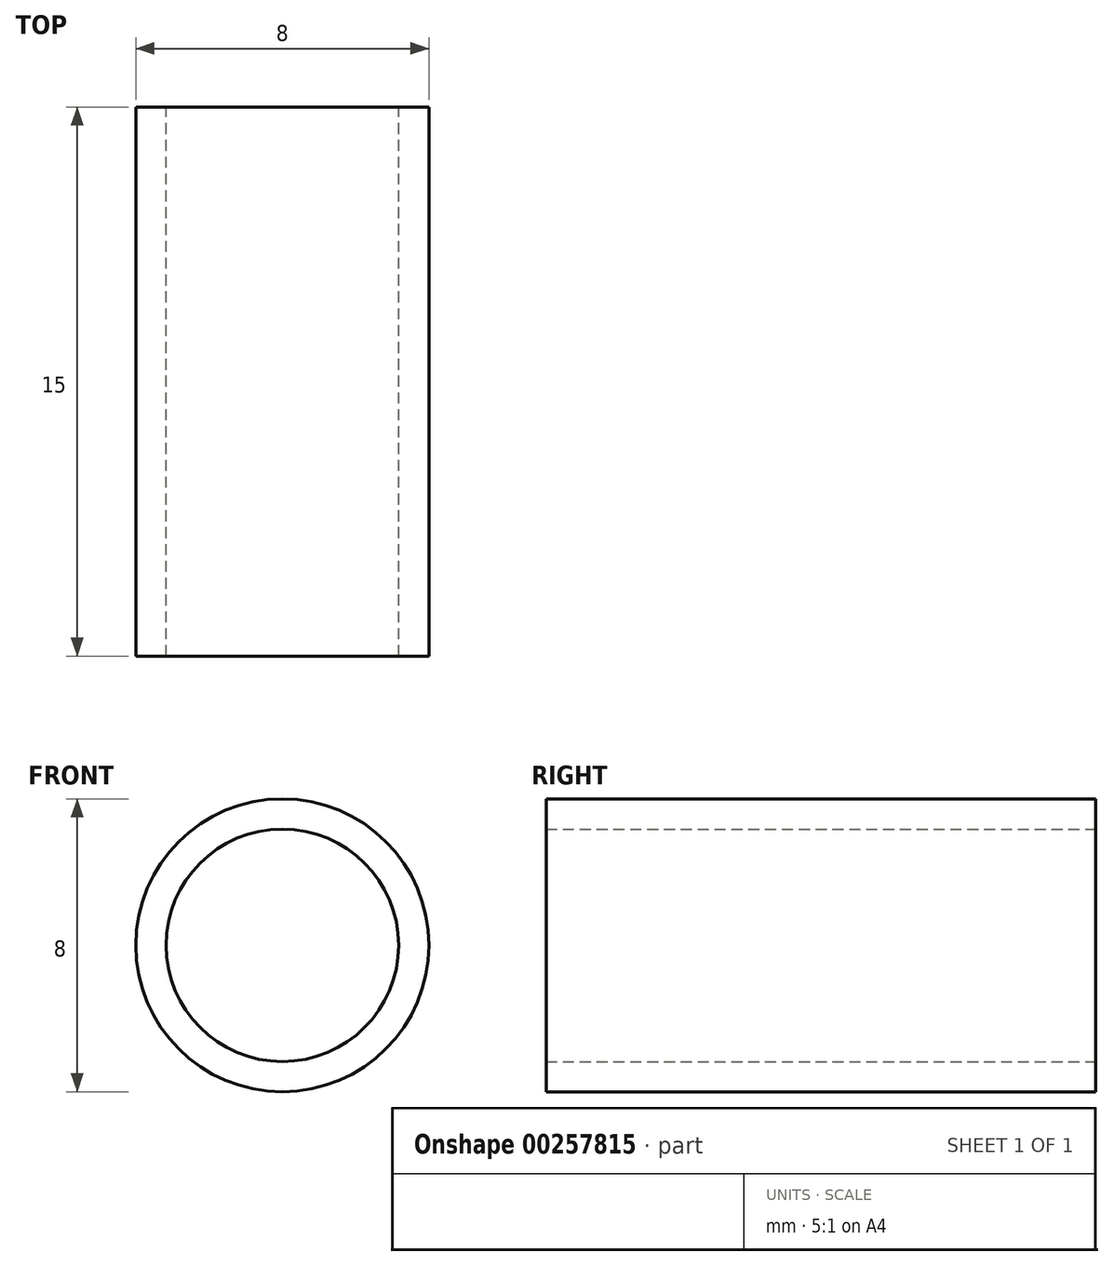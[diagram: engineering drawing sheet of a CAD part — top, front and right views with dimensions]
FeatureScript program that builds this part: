
annotation { "Feature Type Name" : "Feature", "Feature Type Description" : "" }
export const myFeature = defineFeature(function(context is Context, id is Id, definition is map)
    precondition{}
    {
        {
            var Q0;
            Q0=qCreatedBy(makeId("Front.planeOp"),FACE);
            var sketch = newSketch(context, id + "F0", { "sketchPlane" : qUnion([Q0])});
            skCircle(sketch, "E0", {"center": v(0, 0) * mm, "radius": 3.17 * mm});
            skCircle(sketch, "E1", {"center": v(0, 0) * mm, "radius": 4 * mm});
            skSolve(sketch);
        }
        {
            var Q0;
            Q0 = qSketchRegion(id + "F0", true);
            extrude(context, id + "F1", {"entities" : qUnion([Q0]), "depth" : 15 * mm});
        }
    });
